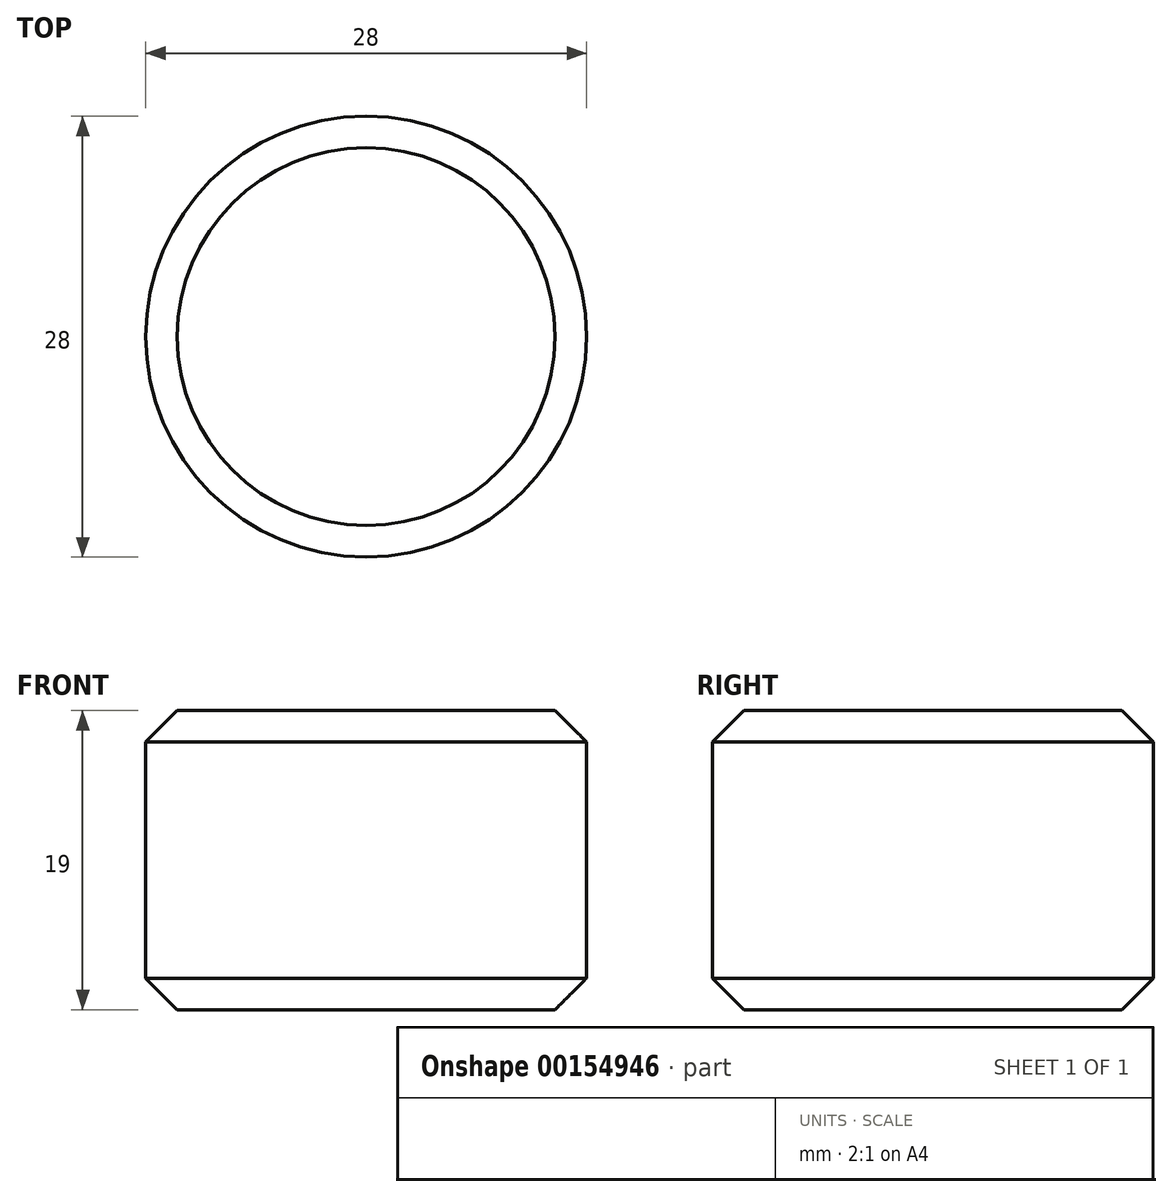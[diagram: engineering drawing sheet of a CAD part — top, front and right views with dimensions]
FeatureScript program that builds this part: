
annotation { "Feature Type Name" : "Feature", "Feature Type Description" : "" }
export const myFeature = defineFeature(function(context is Context, id is Id, definition is map)
    precondition{}
    {
        {
            var Q0;
            Q0=qCreatedBy(makeId("Top.planeOp"),FACE);
            var sketch = newSketch(context, id + "F0", { "sketchPlane" : qUnion([Q0])});
            skCircle(sketch, "E0", {"center": v(0, 0) * mm, "radius": 14 * mm});
            skSolve(sketch);
        }
        {
            var Q0;
            Q0 = qSketchRegion(id + "F0", true);
            extrude(context, id + "F1", {"entities" : qUnion([Q0]), "depth" : 19 * mm});
        }
        {
            var Q0;
            Q0=makeQuery(id+"F1.opExtrude","CAP_EDGE",EDGE,{"disambiguationData":[OSD([sQuery(id+"F0.wireOp",EDGE,"E0")])],"isStart":false});
            var Q1;
            Q1=makeQuery(id+"F1.opExtrude","CAP_EDGE",EDGE,{"disambiguationData":[OSD([sQuery(id+"F0.wireOp",EDGE,"E0")])],"isStart":true});
            chamfer(context, id + "F2", {"entities" : qUnion([Q0, Q1]), "width" : 2 * mm, "tangentPropagation" : true});
        }
    });
